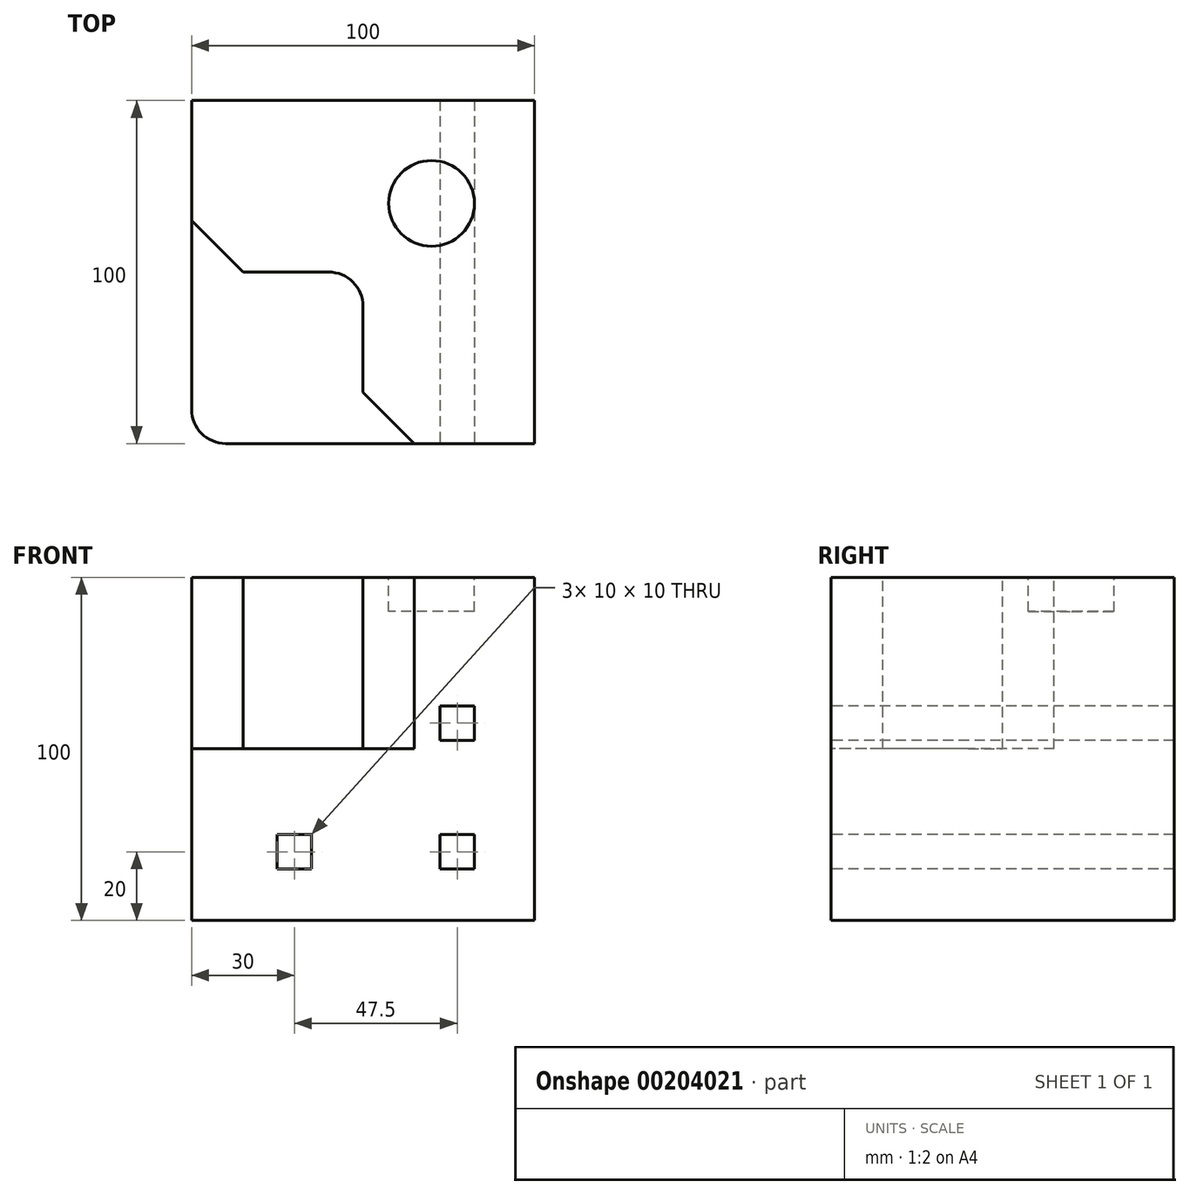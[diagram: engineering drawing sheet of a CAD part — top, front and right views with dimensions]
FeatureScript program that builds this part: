
annotation { "Feature Type Name" : "Feature", "Feature Type Description" : "" }
export const myFeature = defineFeature(function(context is Context, id is Id, definition is map)
    precondition{}
    {
        {
            var Q0;
            Q0=qCreatedBy(makeId("Top.planeOp"),FACE);
            var sketch = newSketch(context, id + "F0", { "sketchPlane" : qUnion([Q0])});
            skLineSegment(sketch, "E0.bottom", {"start": v(0, 0) * mm, "end": v(100, 0) * mm});
            skLineSegment(sketch, "E0.top", {"start": v(10, -100) * mm, "end": v(100, -100) * mm});
            skLineSegment(sketch, "E0.left", {"start": v(0, 0) * mm, "end": v(0, -90) * mm});
            skLineSegment(sketch, "E0.right", {"start": v(100, 0) * mm, "end": v(100, -100) * mm});
            skPoint(sketch, "E1.visualSharp", {"position": v(0, -100) * mm});
            skArc(sketch, "E1.filletArc", {"start": v(0, -90) * mm, "mid": v(2.93, -97.07) * mm, "end": v(10, -100) * mm});
            skSolve(sketch);
        }
        {
            var Q0;
            Q0 = qSketchRegion(id + "F0", true);
            extrude(context, id + "F1", {"entities" : qUnion([Q0]), "depth" : 100 * mm});
        }
        {
            var Q0;
            Q0=makeQuery(id+"F1.opExtrude","CAP_FACE",FACE,{"disambiguationData":[OSD([sQuery(id+"F0.wireOp",EDGE,"E0.bottom"),sQuery(id+"F0.wireOp",EDGE,"E0.top"),sQuery(id+"F0.wireOp",EDGE,"E0.left"),sQuery(id+"F0.wireOp",EDGE,"E0.right"),sQuery(id+"F0.wireOp",EDGE,"E1.filletArc")])],"isStart":false});
            var sketch = newSketch(context, id + "F2", { "sketchPlane" : qUnion([Q0])});
            skLineSegment(sketch, "E2", {"start": v(0, 0) * mm, "end": v(0, -35) * mm});
            skLineSegment(sketch, "E3", {"start": v(0, -35) * mm, "end": v(15, -50) * mm});
            skLineSegment(sketch, "E4", {"start": v(15, -50) * mm, "end": v(40, -50) * mm});
            skLineSegment(sketch, "E5", {"start": v(50, -60) * mm, "end": v(50, -85) * mm});
            skLineSegment(sketch, "E6", {"start": v(50, -85) * mm, "end": v(65, -100) * mm});
            skLineSegment(sketch, "E7", {"start": v(65, -100) * mm, "end": v(100, -100) * mm});
            skLineSegment(sketch, "E8", {"start": v(100, -100) * mm, "end": v(99.67, -101.32) * mm});
            skPoint(sketch, "E9.visualSharp", {"position": v(50, -50) * mm});
            skArc(sketch, "E9.filletArc", {"start": v(50, -60) * mm, "mid": v(47.07, -52.93) * mm, "end": v(40, -50) * mm});
            skSolve(sketch);
        }
        {
            var Q0;
            Q0 = qSketchRegion(id + "F2", true);
            var Q1;
            {var subQ3=sQuery(id+"F2.wireOp",EDGE,"E3");Q1=makeQuery(id+"F2.imprint","IMPRINT",FACE,{"disambiguationData":[TD([[makeQuery(id+"F2.imprint","IMPRINT",EDGE,{"derivedFrom":subQ3}),-1.0]])]});}
            extrude(context, id + "F3", {"entities" : qUnion([Q0, Q1]), "operationType" : NewBodyOperationType.REMOVE, "oppositeDirection" : true, "depth" : 50 * mm});
        }
        {
            var Q0;
            Q0=makeQuery(id+"F1.opExtrude","CAP_FACE",FACE,{"disambiguationData":[OSD([sQuery(id+"F0.wireOp",EDGE,"E0.bottom"),sQuery(id+"F0.wireOp",EDGE,"E0.top"),sQuery(id+"F0.wireOp",EDGE,"E0.left"),sQuery(id+"F0.wireOp",EDGE,"E0.right"),sQuery(id+"F0.wireOp",EDGE,"E1.filletArc")])],"isStart":false});
            var sketch = newSketch(context, id + "F4", { "sketchPlane" : qUnion([Q0])});
            skCircle(sketch, "E10", {"center": v(70, -30) * mm, "radius": 12.5 * mm});
            skSolve(sketch);
        }
        {
            var Q0;
            Q0 = qSketchRegion(id + "F4", true);
            extrude(context, id + "F5", {"entities" : qUnion([Q0]), "operationType" : NewBodyOperationType.REMOVE, "oppositeDirection" : true, "depth" : 10 * mm});
        }
        {
            var Q0;
            Q0=makeQuery(id+"F1.opExtrude","SWEPT_FACE",FACE,{"disambiguationData":[OSD([sQuery(id+"F0.wireOp",EDGE,"E0.top")])]});
            var sketch = newSketch(context, id + "F6", { "sketchPlane" : qUnion([Q0])});
            skLineSegment(sketch, "E11.bottom", {"start": v(25, 25) * mm, "end": v(35, 25) * mm});
            skLineSegment(sketch, "E11.top", {"start": v(25, 15) * mm, "end": v(35, 15) * mm});
            skLineSegment(sketch, "E11.left", {"start": v(25, 25) * mm, "end": v(25, 15) * mm});
            skLineSegment(sketch, "E11.right", {"start": v(35, 25) * mm, "end": v(35, 15) * mm});
            skLineSegment(sketch, "E12.bottom", {"start": v(72.5, 25) * mm, "end": v(82.5, 25) * mm});
            skLineSegment(sketch, "E12.top", {"start": v(72.5, 15) * mm, "end": v(82.5, 15) * mm});
            skLineSegment(sketch, "E12.left", {"start": v(72.5, 25) * mm, "end": v(72.5, 15) * mm});
            skLineSegment(sketch, "E12.right", {"start": v(82.5, 25) * mm, "end": v(82.5, 15) * mm});
            skLineSegment(sketch, "E13.bottom", {"start": v(72.5, 52.5) * mm, "end": v(82.5, 52.5) * mm});
            skLineSegment(sketch, "E13.top", {"start": v(72.5, 62.5) * mm, "end": v(82.5, 62.5) * mm});
            skLineSegment(sketch, "E13.left", {"start": v(72.5, 52.5) * mm, "end": v(72.5, 62.5) * mm});
            skLineSegment(sketch, "E13.right", {"start": v(82.5, 52.5) * mm, "end": v(82.5, 62.5) * mm});
            skSolve(sketch);
        }
        {
            var Q0;
            Q0 = qSketchRegion(id + "F6", true);
            extrude(context, id + "F7", {"entities" : qUnion([Q0]), "operationType" : NewBodyOperationType.REMOVE, "endBound" : BoundingType.THROUGH_ALL, "oppositeDirection" : true, "depth" : 25 * mm});
        }
    });
